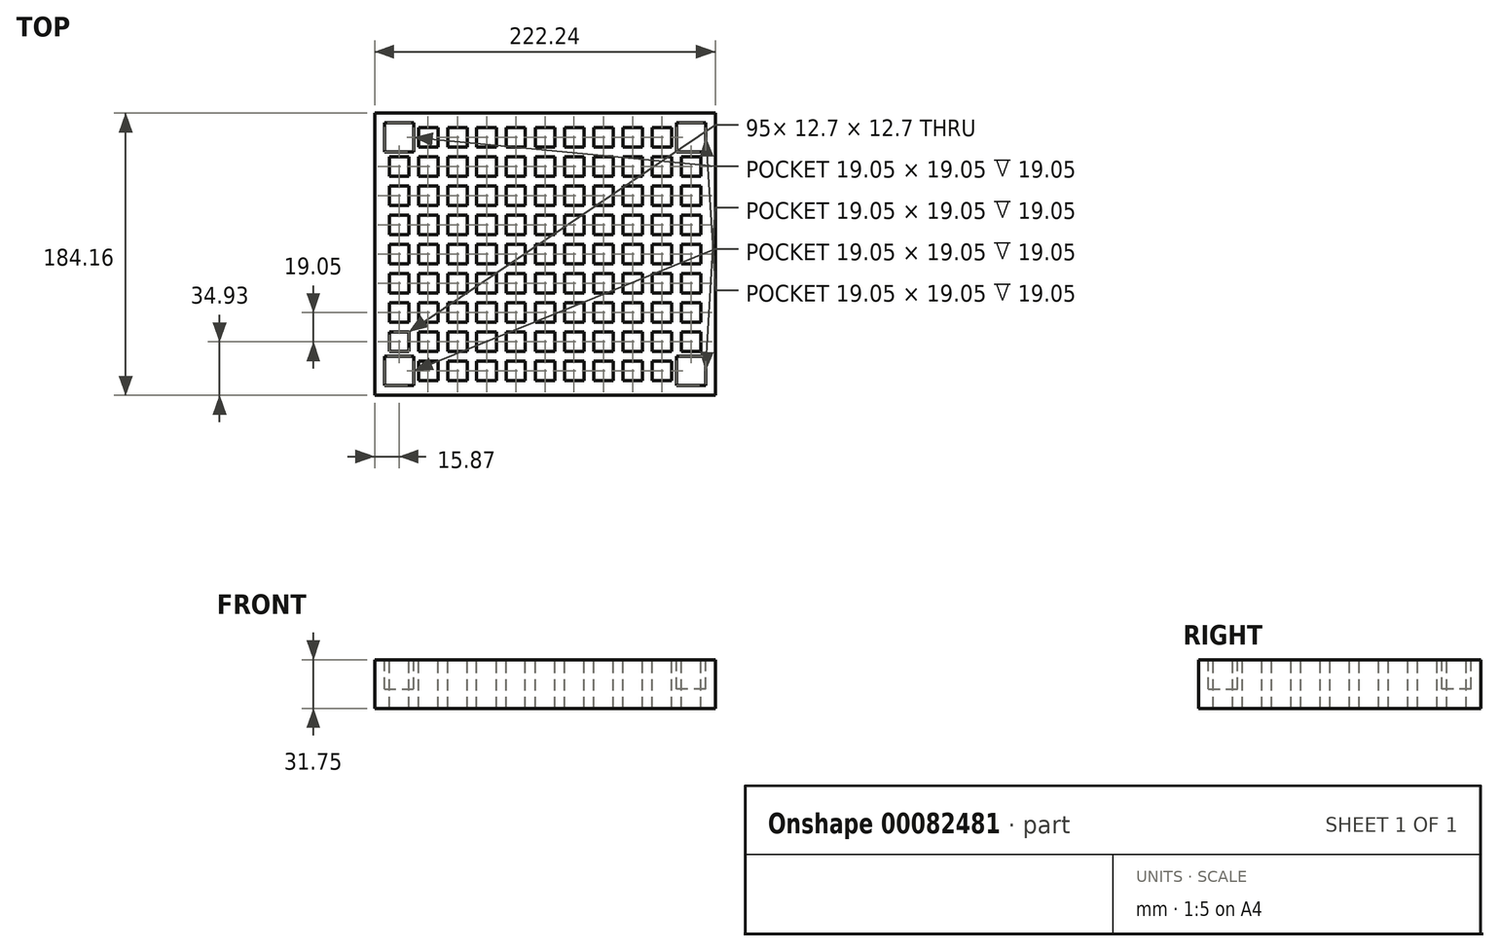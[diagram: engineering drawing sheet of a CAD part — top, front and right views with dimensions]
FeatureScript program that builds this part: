
annotation { "Feature Type Name" : "Feature", "Feature Type Description" : "" }
export const myFeature = defineFeature(function(context is Context, id is Id, definition is map)
    precondition{}
    {
        {
            var Q0;
            Q0=qCreatedBy(makeId("Top.planeOp"),FACE);
            var sketch = newSketch(context, id + "F0", { "sketchPlane" : qUnion([Q0])});
            skLineSegment(sketch, "E0.bottom", {"start": v(111.13, 92.08) * mm, "end": v(-111.12, 92.08) * mm});
            skLineSegment(sketch, "E0.top", {"start": v(111.12, -92.08) * mm, "end": v(-111.13, -92.08) * mm});
            skLineSegment(sketch, "E0.left", {"start": v(111.13, 92.08) * mm, "end": v(111.12, -92.08) * mm});
            skLineSegment(sketch, "E0.right", {"start": v(-111.12, 92.08) * mm, "end": v(-111.13, -92.08) * mm});
            skPoint(sketch, "E0.middle", {"position": v(0, 0) * mm});
            skSolve(sketch);
        }
        {
            var Q0;
            Q0=makeQuery(id+"F0.imprint","IMPRINT",FACE,{"disambiguationData":[TD([[makeQuery(id+"F0.imprint","IMPRINT",EDGE,{"derivedFrom":sQuery(id+"F0.wireOp",EDGE,"E0.bottom")}),1.0]])]});
            extrude(context, id + "F1", {"entities" : qUnion([Q0]), "depth" : 31.75 * mm});
        }
        {
            var Q0;
            Q0=makeQuery(id+"F1.opExtrude","CAP_FACE",FACE,{"disambiguationData":[OSD([sQuery(id+"F0.wireOp",EDGE,"E0.bottom"),sQuery(id+"F0.wireOp",EDGE,"E0.top"),sQuery(id+"F0.wireOp",EDGE,"E0.left"),sQuery(id+"F0.wireOp",EDGE,"E0.right")])],"isStart":false});
            var sketch = newSketch(context, id + "F2", { "sketchPlane" : qUnion([Q0])});
            skLineSegment(sketch, "E1.bottom", {"start": v(-82.55, -69.85) * mm, "end": v(-69.85, -69.85) * mm});
            skLineSegment(sketch, "E1.top", {"start": v(-82.55, -82.55) * mm, "end": v(-69.85, -82.55) * mm});
            skLineSegment(sketch, "E1.left", {"start": v(-82.55, -69.85) * mm, "end": v(-82.55, -82.55) * mm});
            skLineSegment(sketch, "E1.right", {"start": v(-69.85, -69.85) * mm, "end": v(-69.85, -82.55) * mm});
            skLineSegment(sketch, "E2.0.1.0", {"start": v(-82.55, -50.8) * mm, "end": v(-69.85, -50.8) * mm});
            skLineSegment(sketch, "E2.0.1.1", {"start": v(-82.55, -50.8) * mm, "end": v(-82.55, -63.5) * mm});
            skLineSegment(sketch, "E2.0.1.2", {"start": v(-82.55, -63.5) * mm, "end": v(-69.85, -63.5) * mm});
            skLineSegment(sketch, "E2.0.1.3", {"start": v(-69.85, -50.8) * mm, "end": v(-69.85, -63.5) * mm});
            skLineSegment(sketch, "E2.0.2.0", {"start": v(-82.55, -31.75) * mm, "end": v(-69.85, -31.75) * mm});
            skLineSegment(sketch, "E2.0.2.1", {"start": v(-82.55, -31.75) * mm, "end": v(-82.55, -44.45) * mm});
            skLineSegment(sketch, "E2.0.2.2", {"start": v(-82.55, -44.45) * mm, "end": v(-69.85, -44.45) * mm});
            skLineSegment(sketch, "E2.0.2.3", {"start": v(-69.85, -31.75) * mm, "end": v(-69.85, -44.45) * mm});
            skLineSegment(sketch, "E2.0.3.0", {"start": v(-82.55, -12.7) * mm, "end": v(-69.85, -12.7) * mm});
            skLineSegment(sketch, "E2.0.3.1", {"start": v(-82.55, -12.7) * mm, "end": v(-82.55, -25.4) * mm});
            skLineSegment(sketch, "E2.0.3.2", {"start": v(-82.55, -25.4) * mm, "end": v(-69.85, -25.4) * mm});
            skLineSegment(sketch, "E2.0.3.3", {"start": v(-69.85, -12.7) * mm, "end": v(-69.85, -25.4) * mm});
            skLineSegment(sketch, "E2.0.4.0", {"start": v(-82.55, 6.35) * mm, "end": v(-69.85, 6.35) * mm});
            skLineSegment(sketch, "E2.0.4.1", {"start": v(-82.55, 6.35) * mm, "end": v(-82.55, -6.35) * mm});
            skLineSegment(sketch, "E2.0.4.2", {"start": v(-82.55, -6.35) * mm, "end": v(-69.85, -6.35) * mm});
            skLineSegment(sketch, "E2.0.4.3", {"start": v(-69.85, 6.35) * mm, "end": v(-69.85, -6.35) * mm});
            skLineSegment(sketch, "E2.0.5.0", {"start": v(-82.55, 25.4) * mm, "end": v(-69.85, 25.4) * mm});
            skLineSegment(sketch, "E2.0.5.1", {"start": v(-82.55, 25.4) * mm, "end": v(-82.55, 12.7) * mm});
            skLineSegment(sketch, "E2.0.5.2", {"start": v(-82.55, 12.7) * mm, "end": v(-69.85, 12.7) * mm});
            skLineSegment(sketch, "E2.0.5.3", {"start": v(-69.85, 25.4) * mm, "end": v(-69.85, 12.7) * mm});
            skLineSegment(sketch, "E2.0.6.0", {"start": v(-82.55, 44.45) * mm, "end": v(-69.85, 44.45) * mm});
            skLineSegment(sketch, "E2.0.6.1", {"start": v(-82.55, 44.45) * mm, "end": v(-82.55, 31.75) * mm});
            skLineSegment(sketch, "E2.0.6.2", {"start": v(-82.55, 31.75) * mm, "end": v(-69.85, 31.75) * mm});
            skLineSegment(sketch, "E2.0.6.3", {"start": v(-69.85, 44.45) * mm, "end": v(-69.85, 31.75) * mm});
            skLineSegment(sketch, "E2.0.7.0", {"start": v(-82.55, 63.5) * mm, "end": v(-69.85, 63.5) * mm});
            skLineSegment(sketch, "E2.0.7.1", {"start": v(-82.55, 63.5) * mm, "end": v(-82.55, 50.8) * mm});
            skLineSegment(sketch, "E2.0.7.2", {"start": v(-82.55, 50.8) * mm, "end": v(-69.85, 50.8) * mm});
            skLineSegment(sketch, "E2.0.7.3", {"start": v(-69.85, 63.5) * mm, "end": v(-69.85, 50.8) * mm});
            skLineSegment(sketch, "E2.0.8.0", {"start": v(-82.55, 82.55) * mm, "end": v(-69.85, 82.55) * mm});
            skLineSegment(sketch, "E2.0.8.1", {"start": v(-82.55, 82.55) * mm, "end": v(-82.55, 69.85) * mm});
            skLineSegment(sketch, "E2.0.8.2", {"start": v(-82.55, 69.85) * mm, "end": v(-69.85, 69.85) * mm});
            skLineSegment(sketch, "E2.0.8.3", {"start": v(-69.85, 82.55) * mm, "end": v(-69.85, 69.85) * mm});
            skLineSegment(sketch, "E2.1.0.0", {"start": v(-63.5, -69.85) * mm, "end": v(-50.8, -69.85) * mm});
            skLineSegment(sketch, "E2.1.0.1", {"start": v(-63.5, -69.85) * mm, "end": v(-63.5, -82.55) * mm});
            skLineSegment(sketch, "E2.1.0.2", {"start": v(-63.5, -82.55) * mm, "end": v(-50.8, -82.55) * mm});
            skLineSegment(sketch, "E2.1.0.3", {"start": v(-50.8, -69.85) * mm, "end": v(-50.8, -82.55) * mm});
            skLineSegment(sketch, "E2.1.1.0", {"start": v(-63.5, -50.8) * mm, "end": v(-50.8, -50.8) * mm});
            skLineSegment(sketch, "E2.1.1.1", {"start": v(-63.5, -50.8) * mm, "end": v(-63.5, -63.5) * mm});
            skLineSegment(sketch, "E2.1.1.2", {"start": v(-63.5, -63.5) * mm, "end": v(-50.8, -63.5) * mm});
            skLineSegment(sketch, "E2.1.1.3", {"start": v(-50.8, -50.8) * mm, "end": v(-50.8, -63.5) * mm});
            skLineSegment(sketch, "E2.1.2.0", {"start": v(-63.5, -31.75) * mm, "end": v(-50.8, -31.75) * mm});
            skLineSegment(sketch, "E2.1.2.1", {"start": v(-63.5, -31.75) * mm, "end": v(-63.5, -44.45) * mm});
            skLineSegment(sketch, "E2.1.2.2", {"start": v(-63.5, -44.45) * mm, "end": v(-50.8, -44.45) * mm});
            skLineSegment(sketch, "E2.1.2.3", {"start": v(-50.8, -31.75) * mm, "end": v(-50.8, -44.45) * mm});
            skLineSegment(sketch, "E2.1.3.0", {"start": v(-63.5, -12.7) * mm, "end": v(-50.8, -12.7) * mm});
            skLineSegment(sketch, "E2.1.3.1", {"start": v(-63.5, -12.7) * mm, "end": v(-63.5, -25.4) * mm});
            skLineSegment(sketch, "E2.1.3.2", {"start": v(-63.5, -25.4) * mm, "end": v(-50.8, -25.4) * mm});
            skLineSegment(sketch, "E2.1.3.3", {"start": v(-50.8, -12.7) * mm, "end": v(-50.8, -25.4) * mm});
            skLineSegment(sketch, "E2.1.4.0", {"start": v(-63.5, 6.35) * mm, "end": v(-50.8, 6.35) * mm});
            skLineSegment(sketch, "E2.1.4.1", {"start": v(-63.5, 6.35) * mm, "end": v(-63.5, -6.35) * mm});
            skLineSegment(sketch, "E2.1.4.2", {"start": v(-63.5, -6.35) * mm, "end": v(-50.8, -6.35) * mm});
            skLineSegment(sketch, "E2.1.4.3", {"start": v(-50.8, 6.35) * mm, "end": v(-50.8, -6.35) * mm});
            skLineSegment(sketch, "E2.1.5.0", {"start": v(-63.5, 25.4) * mm, "end": v(-50.8, 25.4) * mm});
            skLineSegment(sketch, "E2.1.5.1", {"start": v(-63.5, 25.4) * mm, "end": v(-63.5, 12.7) * mm});
            skLineSegment(sketch, "E2.1.5.2", {"start": v(-63.5, 12.7) * mm, "end": v(-50.8, 12.7) * mm});
            skLineSegment(sketch, "E2.1.5.3", {"start": v(-50.8, 25.4) * mm, "end": v(-50.8, 12.7) * mm});
            skLineSegment(sketch, "E2.1.6.0", {"start": v(-63.5, 44.45) * mm, "end": v(-50.8, 44.45) * mm});
            skLineSegment(sketch, "E2.1.6.1", {"start": v(-63.5, 44.45) * mm, "end": v(-63.5, 31.75) * mm});
            skLineSegment(sketch, "E2.1.6.2", {"start": v(-63.5, 31.75) * mm, "end": v(-50.8, 31.75) * mm});
            skLineSegment(sketch, "E2.1.6.3", {"start": v(-50.8, 44.45) * mm, "end": v(-50.8, 31.75) * mm});
            skLineSegment(sketch, "E2.1.7.0", {"start": v(-63.5, 63.5) * mm, "end": v(-50.8, 63.5) * mm});
            skLineSegment(sketch, "E2.1.7.1", {"start": v(-63.5, 63.5) * mm, "end": v(-63.5, 50.8) * mm});
            skLineSegment(sketch, "E2.1.7.2", {"start": v(-63.5, 50.8) * mm, "end": v(-50.8, 50.8) * mm});
            skLineSegment(sketch, "E2.1.7.3", {"start": v(-50.8, 63.5) * mm, "end": v(-50.8, 50.8) * mm});
            skLineSegment(sketch, "E2.1.8.0", {"start": v(-63.5, 82.55) * mm, "end": v(-50.8, 82.55) * mm});
            skLineSegment(sketch, "E2.1.8.1", {"start": v(-63.5, 82.55) * mm, "end": v(-63.5, 69.85) * mm});
            skLineSegment(sketch, "E2.1.8.2", {"start": v(-63.5, 69.85) * mm, "end": v(-50.8, 69.85) * mm});
            skLineSegment(sketch, "E2.1.8.3", {"start": v(-50.8, 82.55) * mm, "end": v(-50.8, 69.85) * mm});
            skLineSegment(sketch, "E2.2.0.0", {"start": v(-44.45, -69.85) * mm, "end": v(-31.75, -69.85) * mm});
            skLineSegment(sketch, "E2.2.0.1", {"start": v(-44.45, -69.85) * mm, "end": v(-44.45, -82.55) * mm});
            skLineSegment(sketch, "E2.2.0.2", {"start": v(-44.45, -82.55) * mm, "end": v(-31.75, -82.55) * mm});
            skLineSegment(sketch, "E2.2.0.3", {"start": v(-31.75, -69.85) * mm, "end": v(-31.75, -82.55) * mm});
            skLineSegment(sketch, "E2.2.1.0", {"start": v(-44.45, -50.8) * mm, "end": v(-31.75, -50.8) * mm});
            skLineSegment(sketch, "E2.2.1.1", {"start": v(-44.45, -50.8) * mm, "end": v(-44.45, -63.5) * mm});
            skLineSegment(sketch, "E2.2.1.2", {"start": v(-44.45, -63.5) * mm, "end": v(-31.75, -63.5) * mm});
            skLineSegment(sketch, "E2.2.1.3", {"start": v(-31.75, -50.8) * mm, "end": v(-31.75, -63.5) * mm});
            skLineSegment(sketch, "E2.2.2.0", {"start": v(-44.45, -31.75) * mm, "end": v(-31.75, -31.75) * mm});
            skLineSegment(sketch, "E2.2.2.1", {"start": v(-44.45, -31.75) * mm, "end": v(-44.45, -44.45) * mm});
            skLineSegment(sketch, "E2.2.2.2", {"start": v(-44.45, -44.45) * mm, "end": v(-31.75, -44.45) * mm});
            skLineSegment(sketch, "E2.2.2.3", {"start": v(-31.75, -31.75) * mm, "end": v(-31.75, -44.45) * mm});
            skLineSegment(sketch, "E2.2.3.0", {"start": v(-44.45, -12.7) * mm, "end": v(-31.75, -12.7) * mm});
            skLineSegment(sketch, "E2.2.3.1", {"start": v(-44.45, -12.7) * mm, "end": v(-44.45, -25.4) * mm});
            skLineSegment(sketch, "E2.2.3.2", {"start": v(-44.45, -25.4) * mm, "end": v(-31.75, -25.4) * mm});
            skLineSegment(sketch, "E2.2.3.3", {"start": v(-31.75, -12.7) * mm, "end": v(-31.75, -25.4) * mm});
            skLineSegment(sketch, "E2.2.4.0", {"start": v(-44.45, 6.35) * mm, "end": v(-31.75, 6.35) * mm});
            skLineSegment(sketch, "E2.2.4.1", {"start": v(-44.45, 6.35) * mm, "end": v(-44.45, -6.35) * mm});
            skLineSegment(sketch, "E2.2.4.2", {"start": v(-44.45, -6.35) * mm, "end": v(-31.75, -6.35) * mm});
            skLineSegment(sketch, "E2.2.4.3", {"start": v(-31.75, 6.35) * mm, "end": v(-31.75, -6.35) * mm});
            skLineSegment(sketch, "E2.2.5.0", {"start": v(-44.45, 25.4) * mm, "end": v(-31.75, 25.4) * mm});
            skLineSegment(sketch, "E2.2.5.1", {"start": v(-44.45, 25.4) * mm, "end": v(-44.45, 12.7) * mm});
            skLineSegment(sketch, "E2.2.5.2", {"start": v(-44.45, 12.7) * mm, "end": v(-31.75, 12.7) * mm});
            skLineSegment(sketch, "E2.2.5.3", {"start": v(-31.75, 25.4) * mm, "end": v(-31.75, 12.7) * mm});
            skLineSegment(sketch, "E2.2.6.0", {"start": v(-44.45, 44.45) * mm, "end": v(-31.75, 44.45) * mm});
            skLineSegment(sketch, "E2.2.6.1", {"start": v(-44.45, 44.45) * mm, "end": v(-44.45, 31.75) * mm});
            skLineSegment(sketch, "E2.2.6.2", {"start": v(-44.45, 31.75) * mm, "end": v(-31.75, 31.75) * mm});
            skLineSegment(sketch, "E2.2.6.3", {"start": v(-31.75, 44.45) * mm, "end": v(-31.75, 31.75) * mm});
            skLineSegment(sketch, "E2.2.7.0", {"start": v(-44.45, 63.5) * mm, "end": v(-31.75, 63.5) * mm});
            skLineSegment(sketch, "E2.2.7.1", {"start": v(-44.45, 63.5) * mm, "end": v(-44.45, 50.8) * mm});
            skLineSegment(sketch, "E2.2.7.2", {"start": v(-44.45, 50.8) * mm, "end": v(-31.75, 50.8) * mm});
            skLineSegment(sketch, "E2.2.7.3", {"start": v(-31.75, 63.5) * mm, "end": v(-31.75, 50.8) * mm});
            skLineSegment(sketch, "E2.2.8.0", {"start": v(-44.45, 82.55) * mm, "end": v(-31.75, 82.55) * mm});
            skLineSegment(sketch, "E2.2.8.1", {"start": v(-44.45, 82.55) * mm, "end": v(-44.45, 69.85) * mm});
            skLineSegment(sketch, "E2.2.8.2", {"start": v(-44.45, 69.85) * mm, "end": v(-31.75, 69.85) * mm});
            skLineSegment(sketch, "E2.2.8.3", {"start": v(-31.75, 82.55) * mm, "end": v(-31.75, 69.85) * mm});
            skLineSegment(sketch, "E2.3.0.0", {"start": v(-25.4, -69.85) * mm, "end": v(-12.7, -69.85) * mm});
            skLineSegment(sketch, "E2.3.0.1", {"start": v(-25.4, -69.85) * mm, "end": v(-25.4, -82.55) * mm});
            skLineSegment(sketch, "E2.3.0.2", {"start": v(-25.4, -82.55) * mm, "end": v(-12.7, -82.55) * mm});
            skLineSegment(sketch, "E2.3.0.3", {"start": v(-12.7, -69.85) * mm, "end": v(-12.7, -82.55) * mm});
            skLineSegment(sketch, "E2.3.1.0", {"start": v(-25.4, -50.8) * mm, "end": v(-12.7, -50.8) * mm});
            skLineSegment(sketch, "E2.3.1.1", {"start": v(-25.4, -50.8) * mm, "end": v(-25.4, -63.5) * mm});
            skLineSegment(sketch, "E2.3.1.2", {"start": v(-25.4, -63.5) * mm, "end": v(-12.7, -63.5) * mm});
            skLineSegment(sketch, "E2.3.1.3", {"start": v(-12.7, -50.8) * mm, "end": v(-12.7, -63.5) * mm});
            skLineSegment(sketch, "E2.3.2.0", {"start": v(-25.4, -31.75) * mm, "end": v(-12.7, -31.75) * mm});
            skLineSegment(sketch, "E2.3.2.1", {"start": v(-25.4, -31.75) * mm, "end": v(-25.4, -44.45) * mm});
            skLineSegment(sketch, "E2.3.2.2", {"start": v(-25.4, -44.45) * mm, "end": v(-12.7, -44.45) * mm});
            skLineSegment(sketch, "E2.3.2.3", {"start": v(-12.7, -31.75) * mm, "end": v(-12.7, -44.45) * mm});
            skLineSegment(sketch, "E2.3.3.0", {"start": v(-25.4, -12.7) * mm, "end": v(-12.7, -12.7) * mm});
            skLineSegment(sketch, "E2.3.3.1", {"start": v(-25.4, -12.7) * mm, "end": v(-25.4, -25.4) * mm});
            skLineSegment(sketch, "E2.3.3.2", {"start": v(-25.4, -25.4) * mm, "end": v(-12.7, -25.4) * mm});
            skLineSegment(sketch, "E2.3.3.3", {"start": v(-12.7, -12.7) * mm, "end": v(-12.7, -25.4) * mm});
            skLineSegment(sketch, "E2.3.4.0", {"start": v(-25.4, 6.35) * mm, "end": v(-12.7, 6.35) * mm});
            skLineSegment(sketch, "E2.3.4.1", {"start": v(-25.4, 6.35) * mm, "end": v(-25.4, -6.35) * mm});
            skLineSegment(sketch, "E2.3.4.2", {"start": v(-25.4, -6.35) * mm, "end": v(-12.7, -6.35) * mm});
            skLineSegment(sketch, "E2.3.4.3", {"start": v(-12.7, 6.35) * mm, "end": v(-12.7, -6.35) * mm});
            skLineSegment(sketch, "E2.3.5.0", {"start": v(-25.4, 25.4) * mm, "end": v(-12.7, 25.4) * mm});
            skLineSegment(sketch, "E2.3.5.1", {"start": v(-25.4, 25.4) * mm, "end": v(-25.4, 12.7) * mm});
            skLineSegment(sketch, "E2.3.5.2", {"start": v(-25.4, 12.7) * mm, "end": v(-12.7, 12.7) * mm});
            skLineSegment(sketch, "E2.3.5.3", {"start": v(-12.7, 25.4) * mm, "end": v(-12.7, 12.7) * mm});
            skLineSegment(sketch, "E2.3.6.0", {"start": v(-25.4, 44.45) * mm, "end": v(-12.7, 44.45) * mm});
            skLineSegment(sketch, "E2.3.6.1", {"start": v(-25.4, 44.45) * mm, "end": v(-25.4, 31.75) * mm});
            skLineSegment(sketch, "E2.3.6.2", {"start": v(-25.4, 31.75) * mm, "end": v(-12.7, 31.75) * mm});
            skLineSegment(sketch, "E2.3.6.3", {"start": v(-12.7, 44.45) * mm, "end": v(-12.7, 31.75) * mm});
            skLineSegment(sketch, "E2.3.7.0", {"start": v(-25.4, 63.5) * mm, "end": v(-12.7, 63.5) * mm});
            skLineSegment(sketch, "E2.3.7.1", {"start": v(-25.4, 63.5) * mm, "end": v(-25.4, 50.8) * mm});
            skLineSegment(sketch, "E2.3.7.2", {"start": v(-25.4, 50.8) * mm, "end": v(-12.7, 50.8) * mm});
            skLineSegment(sketch, "E2.3.7.3", {"start": v(-12.7, 63.5) * mm, "end": v(-12.7, 50.8) * mm});
            skLineSegment(sketch, "E2.3.8.0", {"start": v(-25.4, 82.55) * mm, "end": v(-12.7, 82.55) * mm});
            skLineSegment(sketch, "E2.3.8.1", {"start": v(-25.4, 82.55) * mm, "end": v(-25.4, 69.85) * mm});
            skLineSegment(sketch, "E2.3.8.2", {"start": v(-25.4, 69.85) * mm, "end": v(-12.7, 69.85) * mm});
            skLineSegment(sketch, "E2.3.8.3", {"start": v(-12.7, 82.55) * mm, "end": v(-12.7, 69.85) * mm});
            skLineSegment(sketch, "E2.4.0.0", {"start": v(-6.35, -69.85) * mm, "end": v(6.35, -69.85) * mm});
            skLineSegment(sketch, "E2.4.0.1", {"start": v(-6.35, -69.85) * mm, "end": v(-6.35, -82.55) * mm});
            skLineSegment(sketch, "E2.4.0.2", {"start": v(-6.35, -82.55) * mm, "end": v(6.35, -82.55) * mm});
            skLineSegment(sketch, "E2.4.0.3", {"start": v(6.35, -69.85) * mm, "end": v(6.35, -82.55) * mm});
            skLineSegment(sketch, "E2.4.1.0", {"start": v(-6.35, -50.8) * mm, "end": v(6.35, -50.8) * mm});
            skLineSegment(sketch, "E2.4.1.1", {"start": v(-6.35, -50.8) * mm, "end": v(-6.35, -63.5) * mm});
            skLineSegment(sketch, "E2.4.1.2", {"start": v(-6.35, -63.5) * mm, "end": v(6.35, -63.5) * mm});
            skLineSegment(sketch, "E2.4.1.3", {"start": v(6.35, -50.8) * mm, "end": v(6.35, -63.5) * mm});
            skLineSegment(sketch, "E2.4.2.0", {"start": v(-6.35, -31.75) * mm, "end": v(6.35, -31.75) * mm});
            skLineSegment(sketch, "E2.4.2.1", {"start": v(-6.35, -31.75) * mm, "end": v(-6.35, -44.45) * mm});
            skLineSegment(sketch, "E2.4.2.2", {"start": v(-6.35, -44.45) * mm, "end": v(6.35, -44.45) * mm});
            skLineSegment(sketch, "E2.4.2.3", {"start": v(6.35, -31.75) * mm, "end": v(6.35, -44.45) * mm});
            skLineSegment(sketch, "E2.4.3.0", {"start": v(-6.35, -12.7) * mm, "end": v(6.35, -12.7) * mm});
            skLineSegment(sketch, "E2.4.3.1", {"start": v(-6.35, -12.7) * mm, "end": v(-6.35, -25.4) * mm});
            skLineSegment(sketch, "E2.4.3.2", {"start": v(-6.35, -25.4) * mm, "end": v(6.35, -25.4) * mm});
            skLineSegment(sketch, "E2.4.3.3", {"start": v(6.35, -12.7) * mm, "end": v(6.35, -25.4) * mm});
            skLineSegment(sketch, "E2.4.4.0", {"start": v(-6.35, 6.35) * mm, "end": v(6.35, 6.35) * mm});
            skLineSegment(sketch, "E2.4.4.1", {"start": v(-6.35, 6.35) * mm, "end": v(-6.35, -6.35) * mm});
            skLineSegment(sketch, "E2.4.4.2", {"start": v(-6.35, -6.35) * mm, "end": v(6.35, -6.35) * mm});
            skLineSegment(sketch, "E2.4.4.3", {"start": v(6.35, 6.35) * mm, "end": v(6.35, -6.35) * mm});
            skLineSegment(sketch, "E2.4.5.0", {"start": v(-6.35, 25.4) * mm, "end": v(6.35, 25.4) * mm});
            skLineSegment(sketch, "E2.4.5.1", {"start": v(-6.35, 25.4) * mm, "end": v(-6.35, 12.7) * mm});
            skLineSegment(sketch, "E2.4.5.2", {"start": v(-6.35, 12.7) * mm, "end": v(6.35, 12.7) * mm});
            skLineSegment(sketch, "E2.4.5.3", {"start": v(6.35, 25.4) * mm, "end": v(6.35, 12.7) * mm});
            skLineSegment(sketch, "E2.4.6.0", {"start": v(-6.35, 44.45) * mm, "end": v(6.35, 44.45) * mm});
            skLineSegment(sketch, "E2.4.6.1", {"start": v(-6.35, 44.45) * mm, "end": v(-6.35, 31.75) * mm});
            skLineSegment(sketch, "E2.4.6.2", {"start": v(-6.35, 31.75) * mm, "end": v(6.35, 31.75) * mm});
            skLineSegment(sketch, "E2.4.6.3", {"start": v(6.35, 44.45) * mm, "end": v(6.35, 31.75) * mm});
            skLineSegment(sketch, "E2.4.7.0", {"start": v(-6.35, 63.5) * mm, "end": v(6.35, 63.5) * mm});
            skLineSegment(sketch, "E2.4.7.1", {"start": v(-6.35, 63.5) * mm, "end": v(-6.35, 50.8) * mm});
            skLineSegment(sketch, "E2.4.7.2", {"start": v(-6.35, 50.8) * mm, "end": v(6.35, 50.8) * mm});
            skLineSegment(sketch, "E2.4.7.3", {"start": v(6.35, 63.5) * mm, "end": v(6.35, 50.8) * mm});
            skLineSegment(sketch, "E2.4.8.0", {"start": v(-6.35, 82.55) * mm, "end": v(6.35, 82.55) * mm});
            skLineSegment(sketch, "E2.4.8.1", {"start": v(-6.35, 82.55) * mm, "end": v(-6.35, 69.85) * mm});
            skLineSegment(sketch, "E2.4.8.2", {"start": v(-6.35, 69.85) * mm, "end": v(6.35, 69.85) * mm});
            skLineSegment(sketch, "E2.4.8.3", {"start": v(6.35, 82.55) * mm, "end": v(6.35, 69.85) * mm});
            skLineSegment(sketch, "E2.5.0.0", {"start": v(12.7, -69.85) * mm, "end": v(25.4, -69.85) * mm});
            skLineSegment(sketch, "E2.5.0.1", {"start": v(12.7, -69.85) * mm, "end": v(12.7, -82.55) * mm});
            skLineSegment(sketch, "E2.5.0.2", {"start": v(12.7, -82.55) * mm, "end": v(25.4, -82.55) * mm});
            skLineSegment(sketch, "E2.5.0.3", {"start": v(25.4, -69.85) * mm, "end": v(25.4, -82.55) * mm});
            skLineSegment(sketch, "E2.5.1.0", {"start": v(12.7, -50.8) * mm, "end": v(25.4, -50.8) * mm});
            skLineSegment(sketch, "E2.5.1.1", {"start": v(12.7, -50.8) * mm, "end": v(12.7, -63.5) * mm});
            skLineSegment(sketch, "E2.5.1.2", {"start": v(12.7, -63.5) * mm, "end": v(25.4, -63.5) * mm});
            skLineSegment(sketch, "E2.5.1.3", {"start": v(25.4, -50.8) * mm, "end": v(25.4, -63.5) * mm});
            skLineSegment(sketch, "E2.5.2.0", {"start": v(12.7, -31.75) * mm, "end": v(25.4, -31.75) * mm});
            skLineSegment(sketch, "E2.5.2.1", {"start": v(12.7, -31.75) * mm, "end": v(12.7, -44.45) * mm});
            skLineSegment(sketch, "E2.5.2.2", {"start": v(12.7, -44.45) * mm, "end": v(25.4, -44.45) * mm});
            skLineSegment(sketch, "E2.5.2.3", {"start": v(25.4, -31.75) * mm, "end": v(25.4, -44.45) * mm});
            skLineSegment(sketch, "E2.5.3.0", {"start": v(12.7, -12.7) * mm, "end": v(25.4, -12.7) * mm});
            skLineSegment(sketch, "E2.5.3.1", {"start": v(12.7, -12.7) * mm, "end": v(12.7, -25.4) * mm});
            skLineSegment(sketch, "E2.5.3.2", {"start": v(12.7, -25.4) * mm, "end": v(25.4, -25.4) * mm});
            skLineSegment(sketch, "E2.5.3.3", {"start": v(25.4, -12.7) * mm, "end": v(25.4, -25.4) * mm});
            skLineSegment(sketch, "E2.5.4.0", {"start": v(12.7, 6.35) * mm, "end": v(25.4, 6.35) * mm});
            skLineSegment(sketch, "E2.5.4.1", {"start": v(12.7, 6.35) * mm, "end": v(12.7, -6.35) * mm});
            skLineSegment(sketch, "E2.5.4.2", {"start": v(12.7, -6.35) * mm, "end": v(25.4, -6.35) * mm});
            skLineSegment(sketch, "E2.5.4.3", {"start": v(25.4, 6.35) * mm, "end": v(25.4, -6.35) * mm});
            skLineSegment(sketch, "E2.5.5.0", {"start": v(12.7, 25.4) * mm, "end": v(25.4, 25.4) * mm});
            skLineSegment(sketch, "E2.5.5.1", {"start": v(12.7, 25.4) * mm, "end": v(12.7, 12.7) * mm});
            skLineSegment(sketch, "E2.5.5.2", {"start": v(12.7, 12.7) * mm, "end": v(25.4, 12.7) * mm});
            skLineSegment(sketch, "E2.5.5.3", {"start": v(25.4, 25.4) * mm, "end": v(25.4, 12.7) * mm});
            skLineSegment(sketch, "E2.5.6.0", {"start": v(12.7, 44.45) * mm, "end": v(25.4, 44.45) * mm});
            skLineSegment(sketch, "E2.5.6.1", {"start": v(12.7, 44.45) * mm, "end": v(12.7, 31.75) * mm});
            skLineSegment(sketch, "E2.5.6.2", {"start": v(12.7, 31.75) * mm, "end": v(25.4, 31.75) * mm});
            skLineSegment(sketch, "E2.5.6.3", {"start": v(25.4, 44.45) * mm, "end": v(25.4, 31.75) * mm});
            skLineSegment(sketch, "E2.5.7.0", {"start": v(12.7, 63.5) * mm, "end": v(25.4, 63.5) * mm});
            skLineSegment(sketch, "E2.5.7.1", {"start": v(12.7, 63.5) * mm, "end": v(12.7, 50.8) * mm});
            skLineSegment(sketch, "E2.5.7.2", {"start": v(12.7, 50.8) * mm, "end": v(25.4, 50.8) * mm});
            skLineSegment(sketch, "E2.5.7.3", {"start": v(25.4, 63.5) * mm, "end": v(25.4, 50.8) * mm});
            skLineSegment(sketch, "E2.5.8.0", {"start": v(12.7, 82.55) * mm, "end": v(25.4, 82.55) * mm});
            skLineSegment(sketch, "E2.5.8.1", {"start": v(12.7, 82.55) * mm, "end": v(12.7, 69.85) * mm});
            skLineSegment(sketch, "E2.5.8.2", {"start": v(12.7, 69.85) * mm, "end": v(25.4, 69.85) * mm});
            skLineSegment(sketch, "E2.5.8.3", {"start": v(25.4, 82.55) * mm, "end": v(25.4, 69.85) * mm});
            skLineSegment(sketch, "E2.6.0.0", {"start": v(31.75, -69.85) * mm, "end": v(44.45, -69.85) * mm});
            skLineSegment(sketch, "E2.6.0.1", {"start": v(31.75, -69.85) * mm, "end": v(31.75, -82.55) * mm});
            skLineSegment(sketch, "E2.6.0.2", {"start": v(31.75, -82.55) * mm, "end": v(44.45, -82.55) * mm});
            skLineSegment(sketch, "E2.6.0.3", {"start": v(44.45, -69.85) * mm, "end": v(44.45, -82.55) * mm});
            skLineSegment(sketch, "E2.6.1.0", {"start": v(31.75, -50.8) * mm, "end": v(44.45, -50.8) * mm});
            skLineSegment(sketch, "E2.6.1.1", {"start": v(31.75, -50.8) * mm, "end": v(31.75, -63.5) * mm});
            skLineSegment(sketch, "E2.6.1.2", {"start": v(31.75, -63.5) * mm, "end": v(44.45, -63.5) * mm});
            skLineSegment(sketch, "E2.6.1.3", {"start": v(44.45, -50.8) * mm, "end": v(44.45, -63.5) * mm});
            skLineSegment(sketch, "E2.6.2.0", {"start": v(31.75, -31.75) * mm, "end": v(44.45, -31.75) * mm});
            skLineSegment(sketch, "E2.6.2.1", {"start": v(31.75, -31.75) * mm, "end": v(31.75, -44.45) * mm});
            skLineSegment(sketch, "E2.6.2.2", {"start": v(31.75, -44.45) * mm, "end": v(44.45, -44.45) * mm});
            skLineSegment(sketch, "E2.6.2.3", {"start": v(44.45, -31.75) * mm, "end": v(44.45, -44.45) * mm});
            skLineSegment(sketch, "E2.6.3.0", {"start": v(31.75, -12.7) * mm, "end": v(44.45, -12.7) * mm});
            skLineSegment(sketch, "E2.6.3.1", {"start": v(31.75, -12.7) * mm, "end": v(31.75, -25.4) * mm});
            skLineSegment(sketch, "E2.6.3.2", {"start": v(31.75, -25.4) * mm, "end": v(44.45, -25.4) * mm});
            skLineSegment(sketch, "E2.6.3.3", {"start": v(44.45, -12.7) * mm, "end": v(44.45, -25.4) * mm});
            skLineSegment(sketch, "E2.6.4.0", {"start": v(31.75, 6.35) * mm, "end": v(44.45, 6.35) * mm});
            skLineSegment(sketch, "E2.6.4.1", {"start": v(31.75, 6.35) * mm, "end": v(31.75, -6.35) * mm});
            skLineSegment(sketch, "E2.6.4.2", {"start": v(31.75, -6.35) * mm, "end": v(44.45, -6.35) * mm});
            skLineSegment(sketch, "E2.6.4.3", {"start": v(44.45, 6.35) * mm, "end": v(44.45, -6.35) * mm});
            skLineSegment(sketch, "E2.6.5.0", {"start": v(31.75, 25.4) * mm, "end": v(44.45, 25.4) * mm});
            skLineSegment(sketch, "E2.6.5.1", {"start": v(31.75, 25.4) * mm, "end": v(31.75, 12.7) * mm});
            skLineSegment(sketch, "E2.6.5.2", {"start": v(31.75, 12.7) * mm, "end": v(44.45, 12.7) * mm});
            skLineSegment(sketch, "E2.6.5.3", {"start": v(44.45, 25.4) * mm, "end": v(44.45, 12.7) * mm});
            skLineSegment(sketch, "E2.6.6.0", {"start": v(31.75, 44.45) * mm, "end": v(44.45, 44.45) * mm});
            skLineSegment(sketch, "E2.6.6.1", {"start": v(31.75, 44.45) * mm, "end": v(31.75, 31.75) * mm});
            skLineSegment(sketch, "E2.6.6.2", {"start": v(31.75, 31.75) * mm, "end": v(44.45, 31.75) * mm});
            skLineSegment(sketch, "E2.6.6.3", {"start": v(44.45, 44.45) * mm, "end": v(44.45, 31.75) * mm});
            skLineSegment(sketch, "E2.6.7.0", {"start": v(31.75, 63.5) * mm, "end": v(44.45, 63.5) * mm});
            skLineSegment(sketch, "E2.6.7.1", {"start": v(31.75, 63.5) * mm, "end": v(31.75, 50.8) * mm});
            skLineSegment(sketch, "E2.6.7.2", {"start": v(31.75, 50.8) * mm, "end": v(44.45, 50.8) * mm});
            skLineSegment(sketch, "E2.6.7.3", {"start": v(44.45, 63.5) * mm, "end": v(44.45, 50.8) * mm});
            skLineSegment(sketch, "E2.6.8.0", {"start": v(31.75, 82.55) * mm, "end": v(44.45, 82.55) * mm});
            skLineSegment(sketch, "E2.6.8.1", {"start": v(31.75, 82.55) * mm, "end": v(31.75, 69.85) * mm});
            skLineSegment(sketch, "E2.6.8.2", {"start": v(31.75, 69.85) * mm, "end": v(44.45, 69.85) * mm});
            skLineSegment(sketch, "E2.6.8.3", {"start": v(44.45, 82.55) * mm, "end": v(44.45, 69.85) * mm});
            skLineSegment(sketch, "E2.7.0.0", {"start": v(50.8, -69.85) * mm, "end": v(63.5, -69.85) * mm});
            skLineSegment(sketch, "E2.7.0.1", {"start": v(50.8, -69.85) * mm, "end": v(50.8, -82.55) * mm});
            skLineSegment(sketch, "E2.7.0.2", {"start": v(50.8, -82.55) * mm, "end": v(63.5, -82.55) * mm});
            skLineSegment(sketch, "E2.7.0.3", {"start": v(63.5, -69.85) * mm, "end": v(63.5, -82.55) * mm});
            skLineSegment(sketch, "E2.7.1.0", {"start": v(50.8, -50.8) * mm, "end": v(63.5, -50.8) * mm});
            skLineSegment(sketch, "E2.7.1.1", {"start": v(50.8, -50.8) * mm, "end": v(50.8, -63.5) * mm});
            skLineSegment(sketch, "E2.7.1.2", {"start": v(50.8, -63.5) * mm, "end": v(63.5, -63.5) * mm});
            skLineSegment(sketch, "E2.7.1.3", {"start": v(63.5, -50.8) * mm, "end": v(63.5, -63.5) * mm});
            skLineSegment(sketch, "E2.7.2.0", {"start": v(50.8, -31.75) * mm, "end": v(63.5, -31.75) * mm});
            skLineSegment(sketch, "E2.7.2.1", {"start": v(50.8, -31.75) * mm, "end": v(50.8, -44.45) * mm});
            skLineSegment(sketch, "E2.7.2.2", {"start": v(50.8, -44.45) * mm, "end": v(63.5, -44.45) * mm});
            skLineSegment(sketch, "E2.7.2.3", {"start": v(63.5, -31.75) * mm, "end": v(63.5, -44.45) * mm});
            skLineSegment(sketch, "E2.7.3.0", {"start": v(50.8, -12.7) * mm, "end": v(63.5, -12.7) * mm});
            skLineSegment(sketch, "E2.7.3.1", {"start": v(50.8, -12.7) * mm, "end": v(50.8, -25.4) * mm});
            skLineSegment(sketch, "E2.7.3.2", {"start": v(50.8, -25.4) * mm, "end": v(63.5, -25.4) * mm});
            skLineSegment(sketch, "E2.7.3.3", {"start": v(63.5, -12.7) * mm, "end": v(63.5, -25.4) * mm});
            skLineSegment(sketch, "E2.7.4.0", {"start": v(50.8, 6.35) * mm, "end": v(63.5, 6.35) * mm});
            skLineSegment(sketch, "E2.7.4.1", {"start": v(50.8, 6.35) * mm, "end": v(50.8, -6.35) * mm});
            skLineSegment(sketch, "E2.7.4.2", {"start": v(50.8, -6.35) * mm, "end": v(63.5, -6.35) * mm});
            skLineSegment(sketch, "E2.7.4.3", {"start": v(63.5, 6.35) * mm, "end": v(63.5, -6.35) * mm});
            skLineSegment(sketch, "E2.7.5.0", {"start": v(50.8, 25.4) * mm, "end": v(63.5, 25.4) * mm});
            skLineSegment(sketch, "E2.7.5.1", {"start": v(50.8, 25.4) * mm, "end": v(50.8, 12.7) * mm});
            skLineSegment(sketch, "E2.7.5.2", {"start": v(50.8, 12.7) * mm, "end": v(63.5, 12.7) * mm});
            skLineSegment(sketch, "E2.7.5.3", {"start": v(63.5, 25.4) * mm, "end": v(63.5, 12.7) * mm});
            skLineSegment(sketch, "E2.7.6.0", {"start": v(50.8, 44.45) * mm, "end": v(63.5, 44.45) * mm});
            skLineSegment(sketch, "E2.7.6.1", {"start": v(50.8, 44.45) * mm, "end": v(50.8, 31.75) * mm});
            skLineSegment(sketch, "E2.7.6.2", {"start": v(50.8, 31.75) * mm, "end": v(63.5, 31.75) * mm});
            skLineSegment(sketch, "E2.7.6.3", {"start": v(63.5, 44.45) * mm, "end": v(63.5, 31.75) * mm});
            skLineSegment(sketch, "E2.7.7.0", {"start": v(50.8, 63.5) * mm, "end": v(63.5, 63.5) * mm});
            skLineSegment(sketch, "E2.7.7.1", {"start": v(50.8, 63.5) * mm, "end": v(50.8, 50.8) * mm});
            skLineSegment(sketch, "E2.7.7.2", {"start": v(50.8, 50.8) * mm, "end": v(63.5, 50.8) * mm});
            skLineSegment(sketch, "E2.7.7.3", {"start": v(63.5, 63.5) * mm, "end": v(63.5, 50.8) * mm});
            skLineSegment(sketch, "E2.7.8.0", {"start": v(50.8, 82.55) * mm, "end": v(63.5, 82.55) * mm});
            skLineSegment(sketch, "E2.7.8.1", {"start": v(50.8, 82.55) * mm, "end": v(50.8, 69.85) * mm});
            skLineSegment(sketch, "E2.7.8.2", {"start": v(50.8, 69.85) * mm, "end": v(63.5, 69.85) * mm});
            skLineSegment(sketch, "E2.7.8.3", {"start": v(63.5, 82.55) * mm, "end": v(63.5, 69.85) * mm});
            skLineSegment(sketch, "E2.direction1", {"start": v(-82.55, -69.85) * mm, "end": v(-63.5, -69.85) * mm, "construction": true});
            skLineSegment(sketch, "E2.direction2", {"start": v(-82.55, -69.85) * mm, "end": v(-82.55, -50.8) * mm, "construction": true});
            skLineSegment(sketch, "E3.0.8.0", {"start": v(69.85, -69.85) * mm, "end": v(82.55, -69.85) * mm});
            skLineSegment(sketch, "E3.3.8.0", {"start": v(69.85, -69.85) * mm, "end": v(69.85, -82.55) * mm});
            skLineSegment(sketch, "E3.6.8.0", {"start": v(69.85, -82.55) * mm, "end": v(82.55, -82.55) * mm});
            skLineSegment(sketch, "E3.9.8.0", {"start": v(82.55, -69.85) * mm, "end": v(82.55, -82.55) * mm});
            skLineSegment(sketch, "E3.0.8.1", {"start": v(69.85, -50.8) * mm, "end": v(82.55, -50.8) * mm});
            skLineSegment(sketch, "E3.3.8.1", {"start": v(69.85, -50.8) * mm, "end": v(69.85, -63.5) * mm});
            skLineSegment(sketch, "E3.6.8.1", {"start": v(69.85, -63.5) * mm, "end": v(82.55, -63.5) * mm});
            skLineSegment(sketch, "E3.9.8.1", {"start": v(82.55, -50.8) * mm, "end": v(82.55, -63.5) * mm});
            skLineSegment(sketch, "E3.0.8.2", {"start": v(69.85, -31.75) * mm, "end": v(82.55, -31.75) * mm});
            skLineSegment(sketch, "E3.3.8.2", {"start": v(69.85, -31.75) * mm, "end": v(69.85, -44.45) * mm});
            skLineSegment(sketch, "E3.6.8.2", {"start": v(69.85, -44.45) * mm, "end": v(82.55, -44.45) * mm});
            skLineSegment(sketch, "E3.9.8.2", {"start": v(82.55, -31.75) * mm, "end": v(82.55, -44.45) * mm});
            skLineSegment(sketch, "E3.0.8.3", {"start": v(69.85, -12.7) * mm, "end": v(82.55, -12.7) * mm});
            skLineSegment(sketch, "E3.3.8.3", {"start": v(69.85, -12.7) * mm, "end": v(69.85, -25.4) * mm});
            skLineSegment(sketch, "E3.6.8.3", {"start": v(69.85, -25.4) * mm, "end": v(82.55, -25.4) * mm});
            skLineSegment(sketch, "E3.9.8.3", {"start": v(82.55, -12.7) * mm, "end": v(82.55, -25.4) * mm});
            skLineSegment(sketch, "E3.0.8.4", {"start": v(69.85, 6.35) * mm, "end": v(82.55, 6.35) * mm});
            skLineSegment(sketch, "E3.3.8.4", {"start": v(69.85, 6.35) * mm, "end": v(69.85, -6.35) * mm});
            skLineSegment(sketch, "E3.6.8.4", {"start": v(69.85, -6.35) * mm, "end": v(82.55, -6.35) * mm});
            skLineSegment(sketch, "E3.9.8.4", {"start": v(82.55, 6.35) * mm, "end": v(82.55, -6.35) * mm});
            skLineSegment(sketch, "E3.0.8.5", {"start": v(69.85, 25.4) * mm, "end": v(82.55, 25.4) * mm});
            skLineSegment(sketch, "E3.3.8.5", {"start": v(69.85, 25.4) * mm, "end": v(69.85, 12.7) * mm});
            skLineSegment(sketch, "E3.6.8.5", {"start": v(69.85, 12.7) * mm, "end": v(82.55, 12.7) * mm});
            skLineSegment(sketch, "E3.9.8.5", {"start": v(82.55, 25.4) * mm, "end": v(82.55, 12.7) * mm});
            skLineSegment(sketch, "E3.0.8.6", {"start": v(69.85, 44.45) * mm, "end": v(82.55, 44.45) * mm});
            skLineSegment(sketch, "E3.3.8.6", {"start": v(69.85, 44.45) * mm, "end": v(69.85, 31.75) * mm});
            skLineSegment(sketch, "E3.6.8.6", {"start": v(69.85, 31.75) * mm, "end": v(82.55, 31.75) * mm});
            skLineSegment(sketch, "E3.9.8.6", {"start": v(82.55, 44.45) * mm, "end": v(82.55, 31.75) * mm});
            skLineSegment(sketch, "E3.0.8.7", {"start": v(69.85, 63.5) * mm, "end": v(82.55, 63.5) * mm});
            skLineSegment(sketch, "E3.3.8.7", {"start": v(69.85, 63.5) * mm, "end": v(69.85, 50.8) * mm});
            skLineSegment(sketch, "E3.6.8.7", {"start": v(69.85, 50.8) * mm, "end": v(82.55, 50.8) * mm});
            skLineSegment(sketch, "E3.9.8.7", {"start": v(82.55, 63.5) * mm, "end": v(82.55, 50.8) * mm});
            skLineSegment(sketch, "E3.0.8.8", {"start": v(69.85, 82.55) * mm, "end": v(82.55, 82.55) * mm});
            skLineSegment(sketch, "E3.3.8.8", {"start": v(69.85, 82.55) * mm, "end": v(69.85, 69.85) * mm});
            skLineSegment(sketch, "E3.6.8.8", {"start": v(69.85, 69.85) * mm, "end": v(82.55, 69.85) * mm});
            skLineSegment(sketch, "E3.9.8.8", {"start": v(82.55, 82.55) * mm, "end": v(82.55, 69.85) * mm});
            skLineSegment(sketch, "E4.bottom", {"start": v(-101.6, -50.8) * mm, "end": v(-88.9, -50.8) * mm});
            skLineSegment(sketch, "E4.top", {"start": v(-101.6, -63.5) * mm, "end": v(-88.9, -63.5) * mm});
            skLineSegment(sketch, "E4.left", {"start": v(-101.6, -50.8) * mm, "end": v(-101.6, -63.5) * mm});
            skLineSegment(sketch, "E4.right", {"start": v(-88.9, -50.8) * mm, "end": v(-88.9, -63.5) * mm});
            skLineSegment(sketch, "E5.0.1.0", {"start": v(-101.6, -31.75) * mm, "end": v(-88.9, -31.75) * mm});
            skLineSegment(sketch, "E5.0.1.1", {"start": v(-101.6, -31.75) * mm, "end": v(-101.6, -44.45) * mm});
            skLineSegment(sketch, "E5.0.1.2", {"start": v(-88.9, -31.75) * mm, "end": v(-88.9, -44.45) * mm});
            skLineSegment(sketch, "E5.0.1.3", {"start": v(-101.6, -44.45) * mm, "end": v(-88.9, -44.45) * mm});
            skLineSegment(sketch, "E5.0.2.0", {"start": v(-101.6, -12.7) * mm, "end": v(-88.9, -12.7) * mm});
            skLineSegment(sketch, "E5.0.2.1", {"start": v(-101.6, -12.7) * mm, "end": v(-101.6, -25.4) * mm});
            skLineSegment(sketch, "E5.0.2.2", {"start": v(-88.9, -12.7) * mm, "end": v(-88.9, -25.4) * mm});
            skLineSegment(sketch, "E5.0.2.3", {"start": v(-101.6, -25.4) * mm, "end": v(-88.9, -25.4) * mm});
            skLineSegment(sketch, "E5.0.3.0", {"start": v(-101.6, 6.35) * mm, "end": v(-88.9, 6.35) * mm});
            skLineSegment(sketch, "E5.0.3.1", {"start": v(-101.6, 6.35) * mm, "end": v(-101.6, -6.35) * mm});
            skLineSegment(sketch, "E5.0.3.2", {"start": v(-88.9, 6.35) * mm, "end": v(-88.9, -6.35) * mm});
            skLineSegment(sketch, "E5.0.3.3", {"start": v(-101.6, -6.35) * mm, "end": v(-88.9, -6.35) * mm});
            skLineSegment(sketch, "E5.0.4.0", {"start": v(-101.6, 25.4) * mm, "end": v(-88.9, 25.4) * mm});
            skLineSegment(sketch, "E5.0.4.1", {"start": v(-101.6, 25.4) * mm, "end": v(-101.6, 12.7) * mm});
            skLineSegment(sketch, "E5.0.4.2", {"start": v(-88.9, 25.4) * mm, "end": v(-88.9, 12.7) * mm});
            skLineSegment(sketch, "E5.0.4.3", {"start": v(-101.6, 12.7) * mm, "end": v(-88.9, 12.7) * mm});
            skLineSegment(sketch, "E5.direction1", {"start": v(-101.6, -50.8) * mm, "end": v(-73.03, -50.8) * mm, "construction": true});
            skLineSegment(sketch, "E5.direction2", {"start": v(-101.6, -50.8) * mm, "end": v(-101.6, -31.75) * mm, "construction": true});
            skLineSegment(sketch, "E6", {"start": v(0, 92.08) * mm, "end": v(0, -92.08) * mm});
            skLineSegment(sketch, "E7.MirrorCS", {"start": v(101.6, -50.8) * mm, "end": v(101.6, -31.75) * mm, "construction": true});
            skLineSegment(sketch, "E8.MirrorCS", {"start": v(101.6, -31.75) * mm, "end": v(88.9, -31.75) * mm});
            skLineSegment(sketch, "E9.MirrorCS", {"start": v(101.6, 25.4) * mm, "end": v(101.6, 12.7) * mm});
            skLineSegment(sketch, "E10.MirrorCS", {"start": v(101.6, -44.45) * mm, "end": v(88.9, -44.45) * mm});
            skLineSegment(sketch, "E11.MirrorCS", {"start": v(101.6, -50.8) * mm, "end": v(88.9, -50.8) * mm});
            skLineSegment(sketch, "E12.MirrorCS", {"start": v(101.6, -6.35) * mm, "end": v(88.9, -6.35) * mm});
            skLineSegment(sketch, "E13.MirrorCS", {"start": v(88.9, -31.75) * mm, "end": v(88.9, -44.45) * mm});
            skLineSegment(sketch, "E14.MirrorCS", {"start": v(88.9, 6.35) * mm, "end": v(88.9, -6.35) * mm});
            skLineSegment(sketch, "E15.MirrorCS", {"start": v(101.6, -12.7) * mm, "end": v(88.9, -12.7) * mm});
            skLineSegment(sketch, "E16.MirrorCS", {"start": v(101.6, 25.4) * mm, "end": v(88.9, 25.4) * mm});
            skLineSegment(sketch, "E17.MirrorCS", {"start": v(101.6, -25.4) * mm, "end": v(88.9, -25.4) * mm});
            skLineSegment(sketch, "E18.MirrorCS", {"start": v(101.6, -12.7) * mm, "end": v(101.6, -25.4) * mm});
            skLineSegment(sketch, "E19.MirrorCS", {"start": v(101.6, 6.35) * mm, "end": v(88.9, 6.35) * mm});
            skLineSegment(sketch, "E20.MirrorCS", {"start": v(88.9, -12.7) * mm, "end": v(88.9, -25.4) * mm});
            skLineSegment(sketch, "E21.MirrorCS", {"start": v(101.6, -50.8) * mm, "end": v(101.6, -63.5) * mm});
            skLineSegment(sketch, "E22.MirrorCS", {"start": v(101.6, -63.5) * mm, "end": v(88.9, -63.5) * mm});
            skLineSegment(sketch, "E23.MirrorCS", {"start": v(88.9, 25.4) * mm, "end": v(88.9, 12.7) * mm});
            skLineSegment(sketch, "E24.MirrorCS", {"start": v(88.9, -50.8) * mm, "end": v(88.9, -63.5) * mm});
            skLineSegment(sketch, "E25.MirrorCS", {"start": v(101.6, 12.7) * mm, "end": v(88.9, 12.7) * mm});
            skLineSegment(sketch, "E26.MirrorCS", {"start": v(101.6, -31.75) * mm, "end": v(101.6, -44.45) * mm});
            skLineSegment(sketch, "E27.MirrorCS", {"start": v(101.6, 6.35) * mm, "end": v(101.6, -6.35) * mm});
            skLineSegment(sketch, "E28.0.0.5", {"start": v(-101.6, 44.45) * mm, "end": v(-88.9, 44.45) * mm});
            skLineSegment(sketch, "E28.3.0.5", {"start": v(-101.6, 44.45) * mm, "end": v(-101.6, 31.75) * mm});
            skLineSegment(sketch, "E28.6.0.5", {"start": v(-88.9, 44.45) * mm, "end": v(-88.9, 31.75) * mm});
            skLineSegment(sketch, "E28.9.0.5", {"start": v(-101.6, 31.75) * mm, "end": v(-88.9, 31.75) * mm});
            skLineSegment(sketch, "E28.0.0.6", {"start": v(-101.6, 63.5) * mm, "end": v(-88.9, 63.5) * mm});
            skLineSegment(sketch, "E28.3.0.6", {"start": v(-101.6, 63.5) * mm, "end": v(-101.6, 50.8) * mm});
            skLineSegment(sketch, "E28.6.0.6", {"start": v(-88.9, 63.5) * mm, "end": v(-88.9, 50.8) * mm});
            skLineSegment(sketch, "E28.9.0.6", {"start": v(-101.6, 50.8) * mm, "end": v(-88.9, 50.8) * mm});
            skLineSegment(sketch, "E29.MirrorCS", {"start": v(101.6, 44.45) * mm, "end": v(88.9, 44.45) * mm});
            skLineSegment(sketch, "E30.MirrorCS", {"start": v(101.6, 44.45) * mm, "end": v(101.6, 31.75) * mm});
            skLineSegment(sketch, "E31.MirrorCS", {"start": v(88.9, 44.45) * mm, "end": v(88.9, 31.75) * mm});
            skLineSegment(sketch, "E32.MirrorCS", {"start": v(101.6, 31.75) * mm, "end": v(88.9, 31.75) * mm});
            skLineSegment(sketch, "E33.MirrorCS", {"start": v(101.6, 63.5) * mm, "end": v(88.9, 63.5) * mm});
            skLineSegment(sketch, "E34.MirrorCS", {"start": v(101.6, 63.5) * mm, "end": v(101.6, 50.8) * mm});
            skLineSegment(sketch, "E35.MirrorCS", {"start": v(88.9, 63.5) * mm, "end": v(88.9, 50.8) * mm});
            skLineSegment(sketch, "E36.MirrorCS", {"start": v(101.6, 50.8) * mm, "end": v(88.9, 50.8) * mm});
            skSolve(sketch);
        }
        {
            var Q0;
            Q0=qSketchRegion(id+"F2",true);
            extrude(context, id + "F3", {"entities" : qUnion([Q0]), "operationType" : NewBodyOperationType.REMOVE, "endBound" : BoundingType.THROUGH_ALL, "oppositeDirection" : true, "depth" : 25.4 * mm});
        }
        {
            var Q0;
            Q0=makeQuery(id+"F1.opExtrude","CAP_FACE",FACE,{"disambiguationData":[OSD([sQuery(id+"F0.wireOp",EDGE,"E0.bottom"),sQuery(id+"F0.wireOp",EDGE,"E0.top"),sQuery(id+"F0.wireOp",EDGE,"E0.left"),sQuery(id+"F0.wireOp",EDGE,"E0.right")])],"isStart":false});
            var sketch = newSketch(context, id + "F4", { "sketchPlane" : qUnion([Q0])});
            skLineSegment(sketch, "E37.bottom", {"start": v(-104.78, 85.73) * mm, "end": v(-85.73, 85.73) * mm});
            skLineSegment(sketch, "E37.top", {"start": v(-104.78, 66.67) * mm, "end": v(-85.73, 66.67) * mm});
            skLineSegment(sketch, "E37.left", {"start": v(-104.78, 85.73) * mm, "end": v(-104.78, 66.67) * mm});
            skLineSegment(sketch, "E37.right", {"start": v(-85.73, 85.73) * mm, "end": v(-85.73, 66.67) * mm});
            skLineSegment(sketch, "E38", {"start": v(-111.13, 0) * mm, "end": v(111.13, 0) * mm});
            skLineSegment(sketch, "E39", {"start": v(0, 92.08) * mm, "end": v(0, -92.08) * mm});
            skLineSegment(sketch, "E40.MirrorCS", {"start": v(104.78, 85.72) * mm, "end": v(85.73, 85.72) * mm});
            skLineSegment(sketch, "E41.MirrorCS", {"start": v(104.78, 66.67) * mm, "end": v(85.73, 66.67) * mm});
            skLineSegment(sketch, "E42.MirrorCS", {"start": v(104.78, 85.72) * mm, "end": v(104.78, 66.67) * mm});
            skLineSegment(sketch, "E43.MirrorCS", {"start": v(85.73, 85.72) * mm, "end": v(85.73, 66.67) * mm});
            skLineSegment(sketch, "E44.MirrorCS", {"start": v(-104.78, -85.73) * mm, "end": v(-85.73, -85.73) * mm});
            skLineSegment(sketch, "E45.MirrorCS", {"start": v(-104.78, -66.67) * mm, "end": v(-85.73, -66.67) * mm});
            skLineSegment(sketch, "E46.MirrorCS", {"start": v(-104.78, -85.73) * mm, "end": v(-104.78, -66.67) * mm});
            skLineSegment(sketch, "E47.MirrorCS", {"start": v(-85.73, -85.73) * mm, "end": v(-85.73, -66.67) * mm});
            skLineSegment(sketch, "E48.MirrorCS", {"start": v(104.77, -85.73) * mm, "end": v(104.77, -66.67) * mm});
            skLineSegment(sketch, "E49.MirrorCS", {"start": v(104.77, -66.67) * mm, "end": v(85.72, -66.67) * mm});
            skLineSegment(sketch, "E50.MirrorCS", {"start": v(104.77, -85.73) * mm, "end": v(85.72, -85.73) * mm});
            skLineSegment(sketch, "E51.MirrorCS", {"start": v(85.72, -85.73) * mm, "end": v(85.72, -66.67) * mm});
            skSolve(sketch);
        }
        {
            var Q0;
            Q0=qSketchRegion(id+"F4",true);
            extrude(context, id + "F5", {"entities" : qUnion([Q0]), "operationType" : NewBodyOperationType.REMOVE, "oppositeDirection" : true, "depth" : 19.05 * mm});
        }
    });
